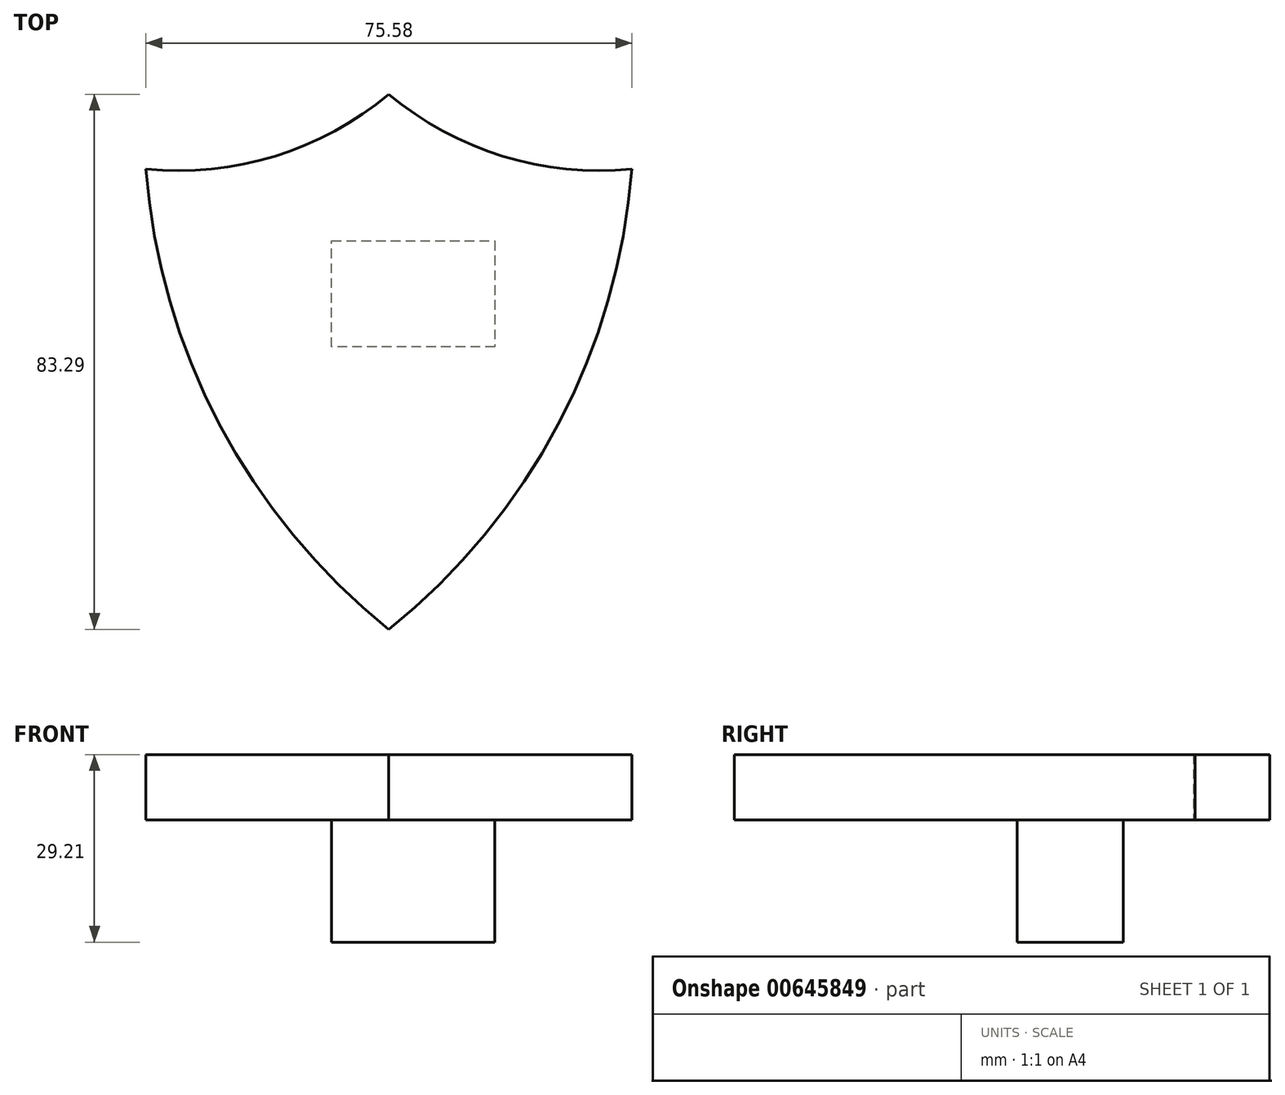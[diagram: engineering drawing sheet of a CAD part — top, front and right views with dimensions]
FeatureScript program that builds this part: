
annotation { "Feature Type Name" : "Feature", "Feature Type Description" : "" }
export const myFeature = defineFeature(function(context is Context, id is Id, definition is map)
    precondition{}
    {
        {
            var Q0;
            Q0=qCreatedBy(makeId("Top.planeOp"),FACE);
            var sketch = newSketch(context, id + "F0", { "sketchPlane" : qUnion([Q0])});
            skArc(sketch, "E0", {"start": v(0, 0) * mm, "mid": v(20.07, 1.98) * mm, "end": v(37.8, 11.61) * mm});
            skArc(sketch, "E1", {"start": v(37.8, 11.61) * mm, "mid": v(55.51, 1.98) * mm, "end": v(75.58, 0) * mm});
            skArc(sketch, "E2", {"start": v(0, 0) * mm, "mid": v(11.44, -39.77) * mm, "end": v(37.8, -71.68) * mm});
            skArc(sketch, "E3", {"start": v(37.8, -71.68) * mm, "mid": v(64.14, -39.77) * mm, "end": v(75.58, 0) * mm});
            skSolve(sketch);
        }
        {
            var Q0;
            Q0=makeQuery(id+"F0.imprint","IMPRINT",FACE,{"disambiguationData":[TD([[makeQuery(id+"F0.imprint","IMPRINT",EDGE,{"derivedFrom":sQuery(id+"F0.wireOp",EDGE,"E0")}),-1.0]])]});
            extrude(context, id + "F1", {"entities" : qUnion([Q0]), "depth" : 10.16 * mm, "offsetDistance" : 25.4 * mm});
        }
        {
            var Q0;
            Q0=makeQuery(id+"F1.opExtrude","CAP_FACE",FACE,{"disambiguationData":[OSD([sQuery(id+"F0.wireOp",EDGE,"E0"),sQuery(id+"F0.wireOp",EDGE,"E1"),sQuery(id+"F0.wireOp",EDGE,"E2"),sQuery(id+"F0.wireOp",EDGE,"E3")])],"isStart":false});
            var sketch = newSketch(context, id + "F2", { "sketchPlane" : qUnion([Q0])});
            skSolve(sketch);
        }
        {
            var Q0;
            Q0=makeQuery(id+"F1.opExtrude","CAP_FACE",FACE,{"disambiguationData":[OSD([sQuery(id+"F0.wireOp",EDGE,"E0"),sQuery(id+"F0.wireOp",EDGE,"E1"),sQuery(id+"F0.wireOp",EDGE,"E2"),sQuery(id+"F0.wireOp",EDGE,"E3")])],"isStart":true});
            var sketch = newSketch(context, id + "F3", { "sketchPlane" : qUnion([Q0])});
            skLineSegment(sketch, "E4", {"start": v(37.8, 11.2) * mm, "end": v(37.8, 27.72) * mm});
            skLineSegment(sketch, "E5", {"start": v(37.8, 27.72) * mm, "end": v(28.9, 27.72) * mm});
            skLineSegment(sketch, "E6", {"start": v(28.9, 27.72) * mm, "end": v(28.9, 11.2) * mm});
            skLineSegment(sketch, "E7", {"start": v(28.9, 11.2) * mm, "end": v(54.3, 11.2) * mm});
            skLineSegment(sketch, "E8", {"start": v(54.3, 11.2) * mm, "end": v(54.3, 27.72) * mm});
            skLineSegment(sketch, "E9", {"start": v(54.3, 27.72) * mm, "end": v(37.8, 27.72) * mm});
            skSolve(sketch);
        }
        {
            var Q0;
            {var subQ0=sQuery(id+"F3.wireOp",EDGE,"E4");Q0=makeQuery(id+"F3.imprint","IMPRINT",FACE,{"disambiguationData":[TD([[makeQuery(id+"F3.imprint","IMPRINT",EDGE,{"derivedFrom":subQ0}),-1.0]])]});}
            var Q1;
            {var subQ0=sQuery(id+"F3.wireOp",EDGE,"E4");Q1=makeQuery(id+"F3.imprint","IMPRINT",FACE,{"disambiguationData":[TD([[makeQuery(id+"F3.imprint","IMPRINT",EDGE,{"derivedFrom":subQ0}),1.0]])]});}
            extrude(context, id + "F4", {"entities" : qUnion([Q0, Q1]), "operationType" : NewBodyOperationType.ADD, "depth" : 19.05 * mm, "offsetDistance" : 25.4 * mm});
        }
    });
